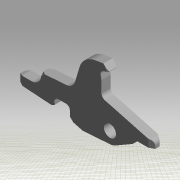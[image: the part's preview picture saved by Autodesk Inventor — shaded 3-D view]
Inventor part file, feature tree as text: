
AUTODESK INVENTOR PART (.ipt)
format: ipt  version: 2018 (Build 220112000, 112)  size: 121,856 bytes
history: native  units: mm (DEFAULTED — no unit token found)
features: fillet x1
ambient origin geometry x8: Origin, YZ Plane, XZ Plane, XY Plane, X Axis, Y Axis, Z Axis, Center Point
bodies: Solid2 (feature_tree), Solid1 (feature_tree)
feature tree (1):
  fillet  "Fillet2"  Radius=0.127mm
